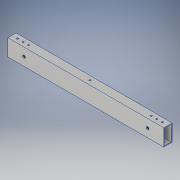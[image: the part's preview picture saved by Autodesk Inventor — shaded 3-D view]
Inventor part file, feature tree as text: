
AUTODESK INVENTOR PART (.ipt)
format: ipt  version: 2019 (Build 230136000, 136)  size: 166,400 bytes
history: native  units: mm
features: sketch x6, hole x4, extrude x2, other x1
ambient origin geometry x8: Origin, YZ Plane, XZ Plane, XY Plane, X Axis, Y Axis, Z Axis, Center Point
bodies: Body1 (feature_tree)
feature tree (13):
  other  "ソリッド1"
  extrude  "押し出し1"  Depth=30.0mm
  hole  "穴1"  [1 undecoded]
  extrude  "押し出し2"  Depth=280.0mm TaperAngle=0.0deg
  hole  "穴2"  [1 undecoded]
  hole  "穴3"  [1 undecoded]
  hole  "穴4"  [1 undecoded]
  sketch  "スケッチ1"
  sketch  "スケッチ2"
  sketch  "スケッチ3"
  sketch  "スケッチ4"
  sketch  "スケッチ5"
  sketch  "スケッチ6"
note: 4 required parameter values undecoded (feature->parameter linkage not recoverable at this tier; creation-order binding heuristic only, values carry confidence <= 0.55)
